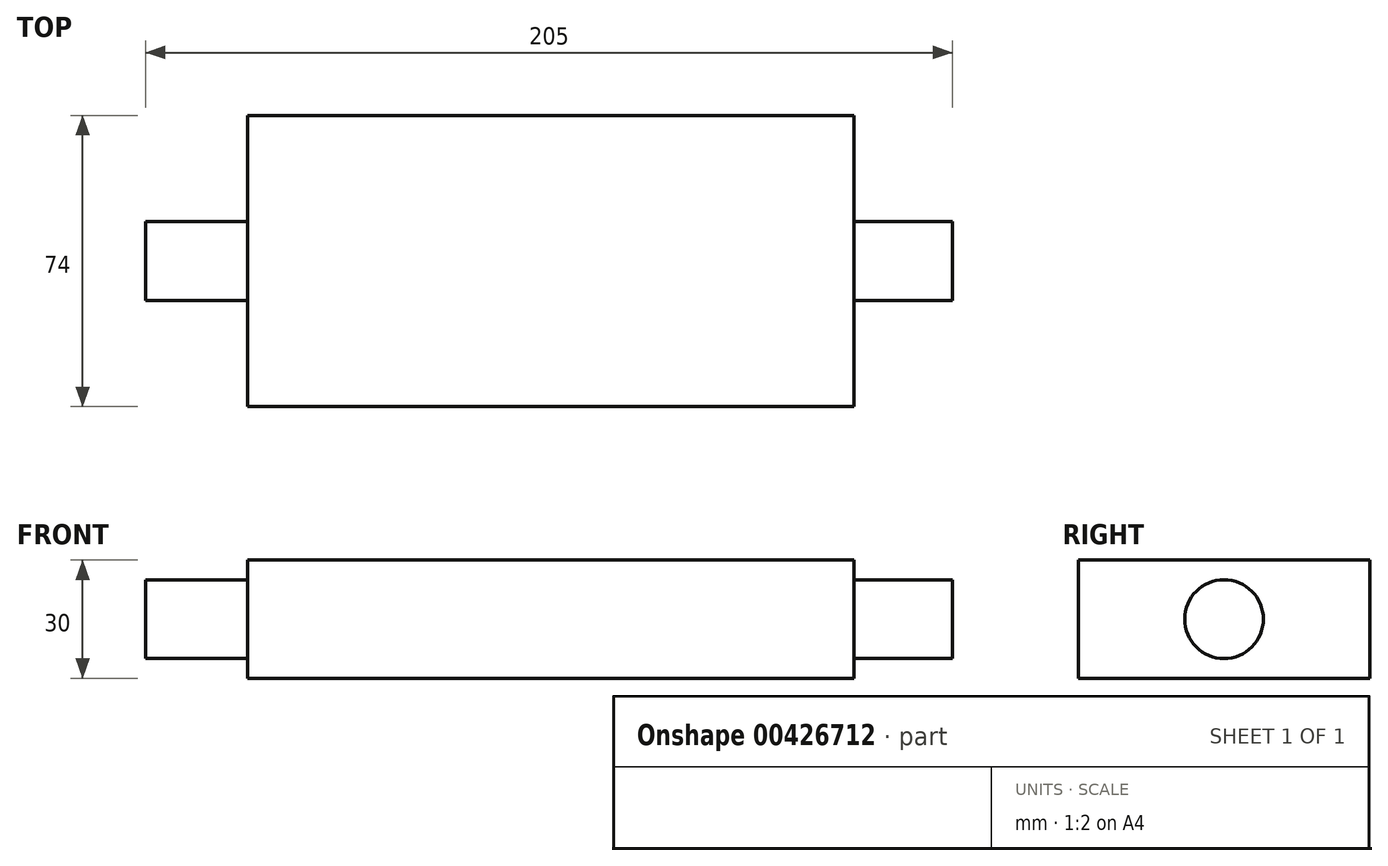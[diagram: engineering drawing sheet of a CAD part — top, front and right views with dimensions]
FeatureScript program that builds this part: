
annotation { "Feature Type Name" : "Feature", "Feature Type Description" : "" }
export const myFeature = defineFeature(function(context is Context, id is Id, definition is map)
    precondition{}
    {
        {
            var Q0;
            Q0=qCreatedBy(makeId("Top.planeOp"),FACE);
            var sketch = newSketch(context, id + "F0", { "sketchPlane" : qUnion([Q0])});
            skLineSegment(sketch, "E0.bottom", {"start": v(77, 37) * mm, "end": v(-77, 37) * mm});
            skLineSegment(sketch, "E0.top", {"start": v(77, -37) * mm, "end": v(-77, -37) * mm});
            skLineSegment(sketch, "E0.left", {"start": v(77, 37) * mm, "end": v(77, -37) * mm});
            skLineSegment(sketch, "E0.right", {"start": v(-77, 37) * mm, "end": v(-77, -37) * mm});
            skPoint(sketch, "E0.middle", {"position": v(0, 0) * mm});
            skSolve(sketch);
        }
        {
            var Q0;
            Q0 = qSketchRegion(id + "F0", true);
            extrude(context, id + "F1", {"entities" : qUnion([Q0]), "depth" : 30 * mm});
        }
        {
            var Q0;
            Q0=makeQuery(id+"F1.opExtrude","SWEPT_FACE",FACE,{"disambiguationData":[OSD([sQuery(id+"F0.wireOp",EDGE,"E0.left")])]});
            var sketch = newSketch(context, id + "F2", { "sketchPlane" : qUnion([Q0])});
            skCircle(sketch, "E1", {"center": v(0, 15) * mm, "radius": 10 * mm});
            skPoint(sketch, "E1.centerSnap0", {"position": v(37, 15) * mm});
            skSolve(sketch);
        }
        {
            var Q0;
            Q0 = qSketchRegion(id + "F2", true);
            extrude(context, id + "F3", {"entities" : qUnion([Q0]), "operationType" : NewBodyOperationType.ADD, "oppositeDirection" : true, "depth" : 180 * mm, "hasSecondDirection" : true, "secondDirectionOppositeDirection" : false, "secondDirectionDepth" : 25 * mm});
        }
    });
